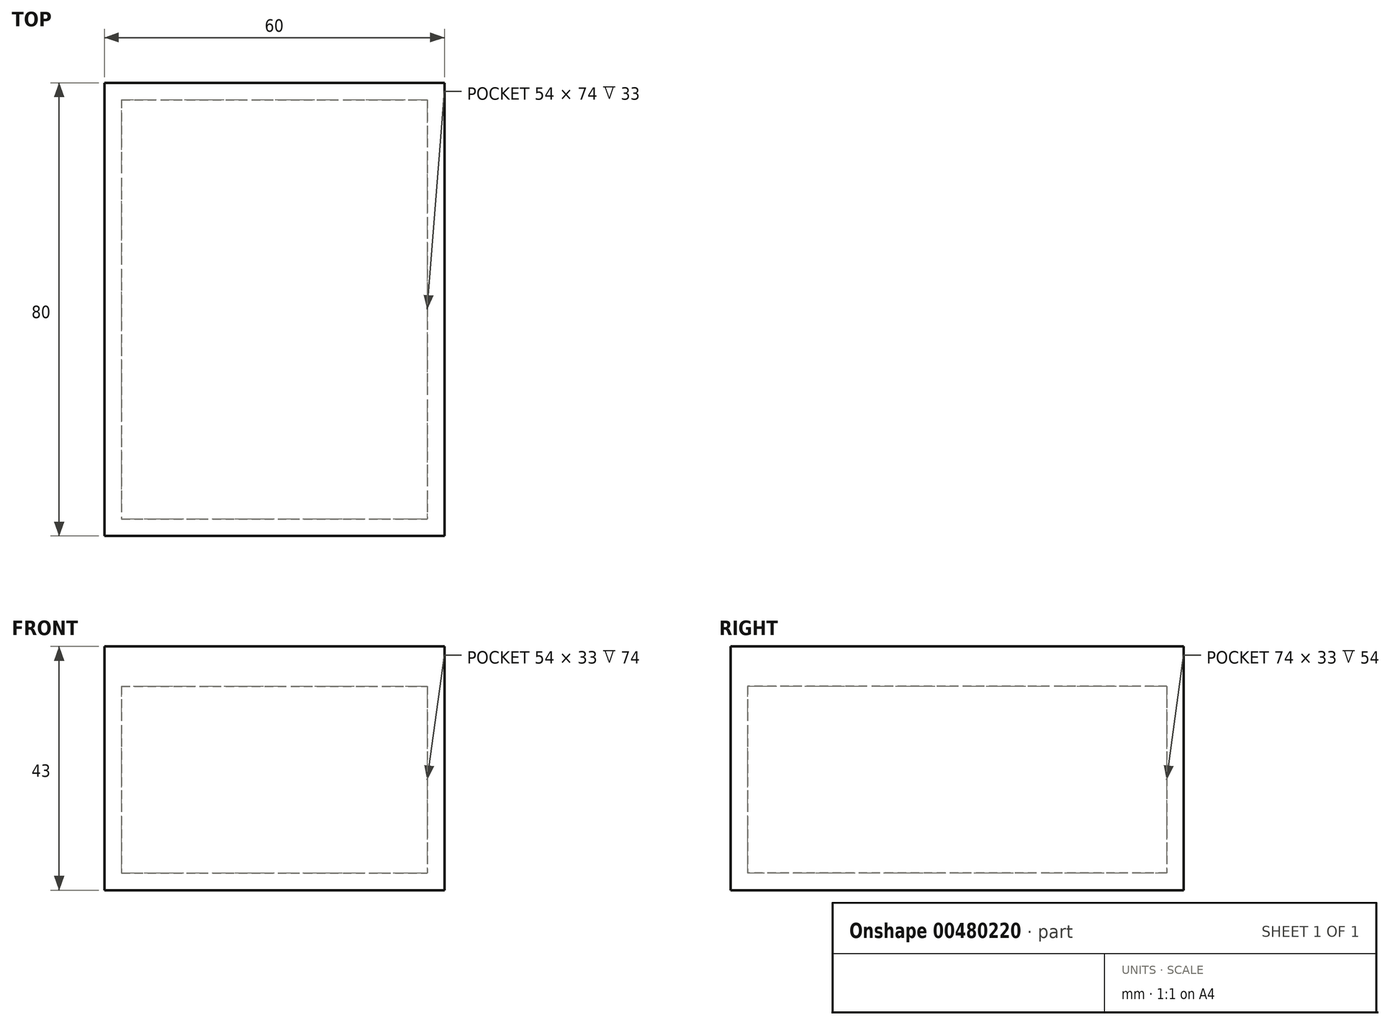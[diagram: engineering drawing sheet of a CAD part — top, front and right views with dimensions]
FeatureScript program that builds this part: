
annotation { "Feature Type Name" : "Feature", "Feature Type Description" : "" }
export const myFeature = defineFeature(function(context is Context, id is Id, definition is map)
    precondition{}
    {
        {
            var Q0;
            Q0=qCreatedBy(makeId("Top.planeOp"),FACE);
            var sketch = newSketch(context, id + "F0", { "sketchPlane" : qUnion([Q0])});
            skLineSegment(sketch, "E0.bottom", {"start": v(-30, 40) * mm, "end": v(30, 40) * mm});
            skLineSegment(sketch, "E0.top", {"start": v(-30, -40) * mm, "end": v(30, -40) * mm});
            skLineSegment(sketch, "E0.left", {"start": v(-30, 40) * mm, "end": v(-30, -40) * mm});
            skLineSegment(sketch, "E0.right", {"start": v(30, 40) * mm, "end": v(30, -40) * mm});
            skPoint(sketch, "E0.middle", {"position": v(0, 0) * mm});
            skSolve(sketch);
        }
        {
            var Q0;
            Q0=makeQuery(id+"F0.imprint","IMPRINT",FACE,{"disambiguationData":[TD([[makeQuery(id+"F0.imprint","IMPRINT",EDGE,{"derivedFrom":sQuery(id+"F0.wireOp",EDGE,"E0.bottom")}),-1.0]])]});
            extrude(context, id + "F1", {"entities" : qUnion([Q0]), "depth" : 40 * mm});
        }
        {
            var Q0;
            Q0=makeQuery(id+"F1.opExtrude","CAP_FACE",FACE,{"disambiguationData":[OSD([sQuery(id+"F0.wireOp",EDGE,"E0.bottom"),sQuery(id+"F0.wireOp",EDGE,"E0.top"),sQuery(id+"F0.wireOp",EDGE,"E0.left"),sQuery(id+"F0.wireOp",EDGE,"E0.right")])],"isStart":false});
            shell(context, id + "F2", {"entities" : qUnion([Q0]), "thickness" : 3 * mm});
        }
        {
            var Q0;
            Q0=makeQuery(id+"F1.opExtrude","CAP_FACE",FACE,{"disambiguationData":[OSD([sQuery(id+"F0.wireOp",EDGE,"E0.bottom"),sQuery(id+"F0.wireOp",EDGE,"E0.top"),sQuery(id+"F0.wireOp",EDGE,"E0.left"),sQuery(id+"F0.wireOp",EDGE,"E0.right")])],"isStart":false});
            var sketch = newSketch(context, id + "F3", { "sketchPlane" : qUnion([Q0])});
            skLineSegment(sketch, "E1.bottom", {"start": v(27, 37) * mm, "end": v(-27, 37) * mm});
            skLineSegment(sketch, "E1.top", {"start": v(27, -37) * mm, "end": v(-27, -37) * mm});
            skLineSegment(sketch, "E1.left", {"start": v(27, 37) * mm, "end": v(27, -37) * mm});
            skLineSegment(sketch, "E1.right", {"start": v(-27, 37) * mm, "end": v(-27, -37) * mm});
            skLineSegment(sketch, "E2.bottom", {"start": v(-30, 40) * mm, "end": v(30, 40) * mm});
            skLineSegment(sketch, "E2.top", {"start": v(-30, -40) * mm, "end": v(30, -40) * mm});
            skLineSegment(sketch, "E2.left", {"start": v(-30, 40) * mm, "end": v(-30, -40) * mm});
            skLineSegment(sketch, "E2.right", {"start": v(30, 40) * mm, "end": v(30, -40) * mm});
            skSolve(sketch);
        }
        {
            var Q0;
            Q0=makeQuery(id+"F3.imprint","IMPRINT",FACE,{"disambiguationData":[TD([[makeQuery(id+"F3.imprint","IMPRINT",EDGE,{"derivedFrom":sQuery(id+"F3.wireOp",EDGE,"E1.bottom")}),1.0]])]});
            var Q1;
            Q1=makeQuery(id+"F3.imprint","IMPRINT",FACE,{"disambiguationData":[TD([[makeQuery(id+"F3.imprint","IMPRINT",EDGE,{"derivedFrom":sQuery(id+"F3.wireOp",EDGE,"E1.bottom")}),-1.0]])]});
            extrude(context, id + "F4", {"entities" : qUnion([Q0, Q1]), "depth" : 3 * mm});
        }
        {
            var Q0;
            Q0=makeQuery(id+"F3.imprint","IMPRINT",FACE,{"disambiguationData":[TD([[makeQuery(id+"F3.imprint","IMPRINT",EDGE,{"derivedFrom":sQuery(id+"F3.wireOp",EDGE,"E1.bottom")}),-1.0]])]});
            extrude(context, id + "F5", {"entities" : qUnion([Q0]), "operationType" : NewBodyOperationType.ADD, "oppositeDirection" : true, "depth" : 4 * mm});
        }
        {
            var Q0;
            Q0=makeQuery(id+"F3.imprint","IMPRINT",FACE,{"disambiguationData":[TD([[makeQuery(id+"F3.imprint","IMPRINT",EDGE,{"derivedFrom":sQuery(id+"F3.wireOp",EDGE,"E1.bottom")}),-1.0]])]});
            var sketch = newSketch(context, id + "F6", { "sketchPlane" : qUnion([Q0])});
            skCircle(sketch, "E3", {"center": v(24, 33) * mm, "radius": 1.5 * mm});
            skCircle(sketch, "E4", {"center": v(24, -33) * mm, "radius": 1.5 * mm});
            skCircle(sketch, "E5", {"center": v(-21, 33) * mm, "radius": 1.5 * mm});
            skCircle(sketch, "E6", {"center": v(-24, -33) * mm, "radius": 1.5 * mm});
            skSolve(sketch);
        }
        {
            var Q0;
            Q0=sQuery(id+"F6.wireOp",EDGE,"E5");
            var Q1;
            Q1=sQuery(id+"F6.wireOp",EDGE,"E3");
            var Q2;
            Q2=sQuery(id+"F6.wireOp",EDGE,"E4");
            var Q3;
            Q3=sQuery(id+"F6.wireOp",EDGE,"E6");
            extrude(context, id + "F7", {"bodyType" : ToolBodyType.SURFACE, "surfaceEntities" : qUnion([Q0, Q1, Q2, Q3]), "depth" : 10 * mm});
        }
    });
